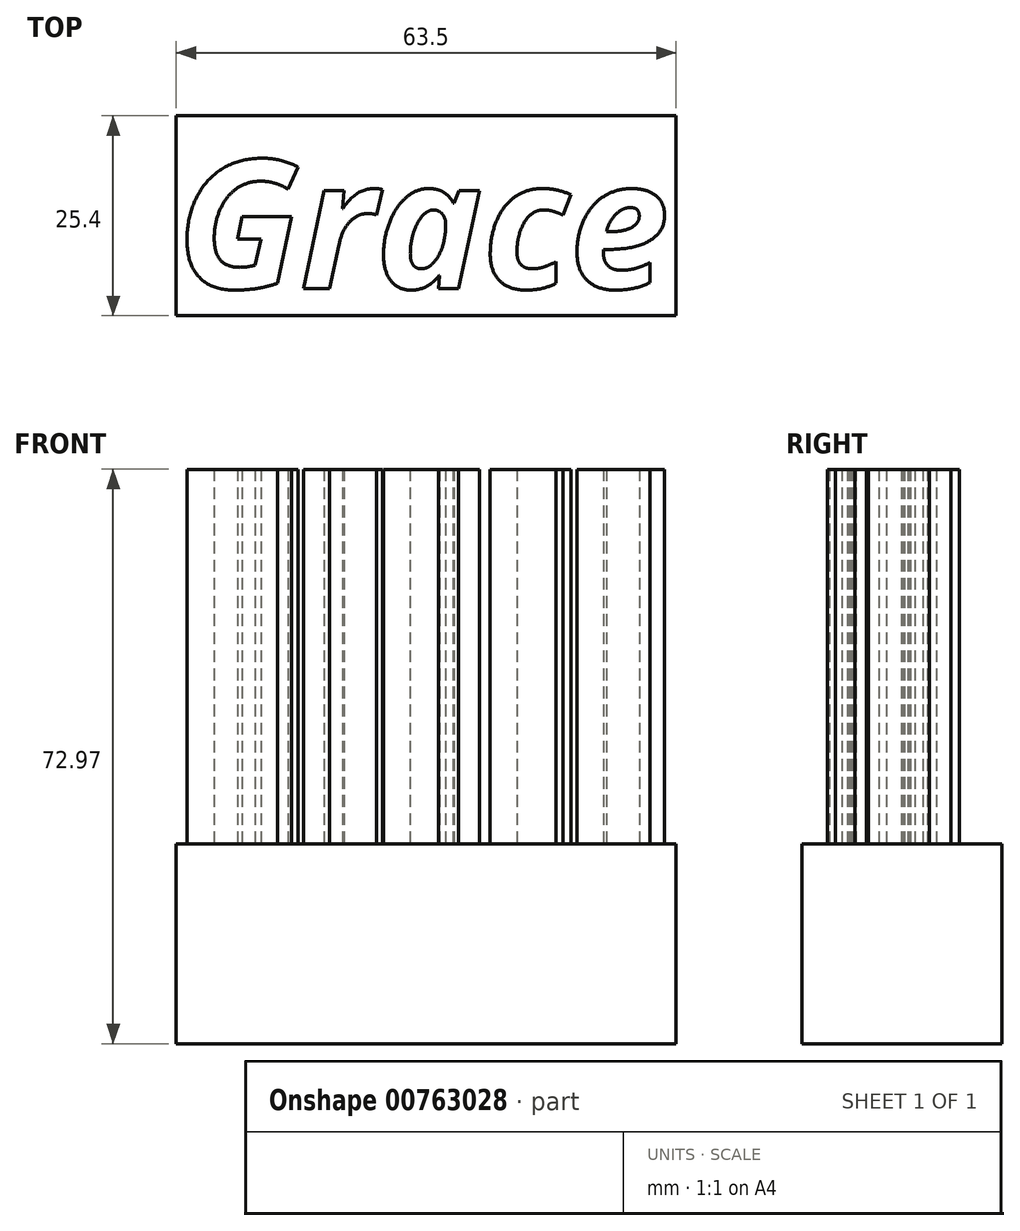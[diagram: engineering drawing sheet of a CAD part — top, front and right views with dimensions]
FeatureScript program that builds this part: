
annotation { "Feature Type Name" : "Feature", "Feature Type Description" : "" }
export const myFeature = defineFeature(function(context is Context, id is Id, definition is map)
    precondition{}
    {
        {
            var Q0;
            Q0=qCreatedBy(makeId("Top.planeOp"),FACE);
            var sketch = newSketch(context, id + "F0", { "sketchPlane" : qUnion([Q0])});
            skLineSegment(sketch, "E0.bottom", {"start": v(0, 0) * mm, "end": v(63.5, 0) * mm});
            skLineSegment(sketch, "E0.top", {"start": v(0, 25.4) * mm, "end": v(63.5, 25.4) * mm});
            skLineSegment(sketch, "E0.left", {"start": v(0, 0) * mm, "end": v(0, 25.4) * mm});
            skLineSegment(sketch, "E0.right", {"start": v(63.5, 0) * mm, "end": v(63.5, 25.4) * mm});
            skSolve(sketch);
        }
        {
            var Q0;
            Q0=makeQuery(id+"F0.imprint","IMPRINT",FACE,{"disambiguationData":[TD([[makeQuery(id+"F0.imprint","IMPRINT",EDGE,{"derivedFrom":sQuery(id+"F0.wireOp",EDGE,"E0.bottom")}),1.0]])]});
            var sketch = newSketch(context, id + "F1", { "sketchPlane" : qUnion([Q0])});
            skText(sketch, "E1", { "text": "Grace", "fontName": "OpenSans-BoldItalic.ttf"});
            const initialGuessF1  = {"E1": [0, 0.00348, 1, 0, 0.01642]};
            skSetInitialGuess(sketch, initialGuessF1);
            skSolve(sketch);
        }
        {
            var Q0;
            Q0 = qSketchRegion(id + "F0", true);
            extrude(context, id + "F2", {"entities" : qUnion([Q0]), "depth" : 25.4 * mm, "offsetDistance" : 25.4 * mm});
        }
        {
            var Q0;
            Q0 = qSketchRegion(id + "F1", true);
            extrude(context, id + "F3", {"entities" : qUnion([Q0]), "operationType" : NewBodyOperationType.ADD, "endBound" : BoundingType.THROUGH_ALL, "depth" : 25.4 * mm, "offsetDistance" : 25.4 * mm});
        }
    });
